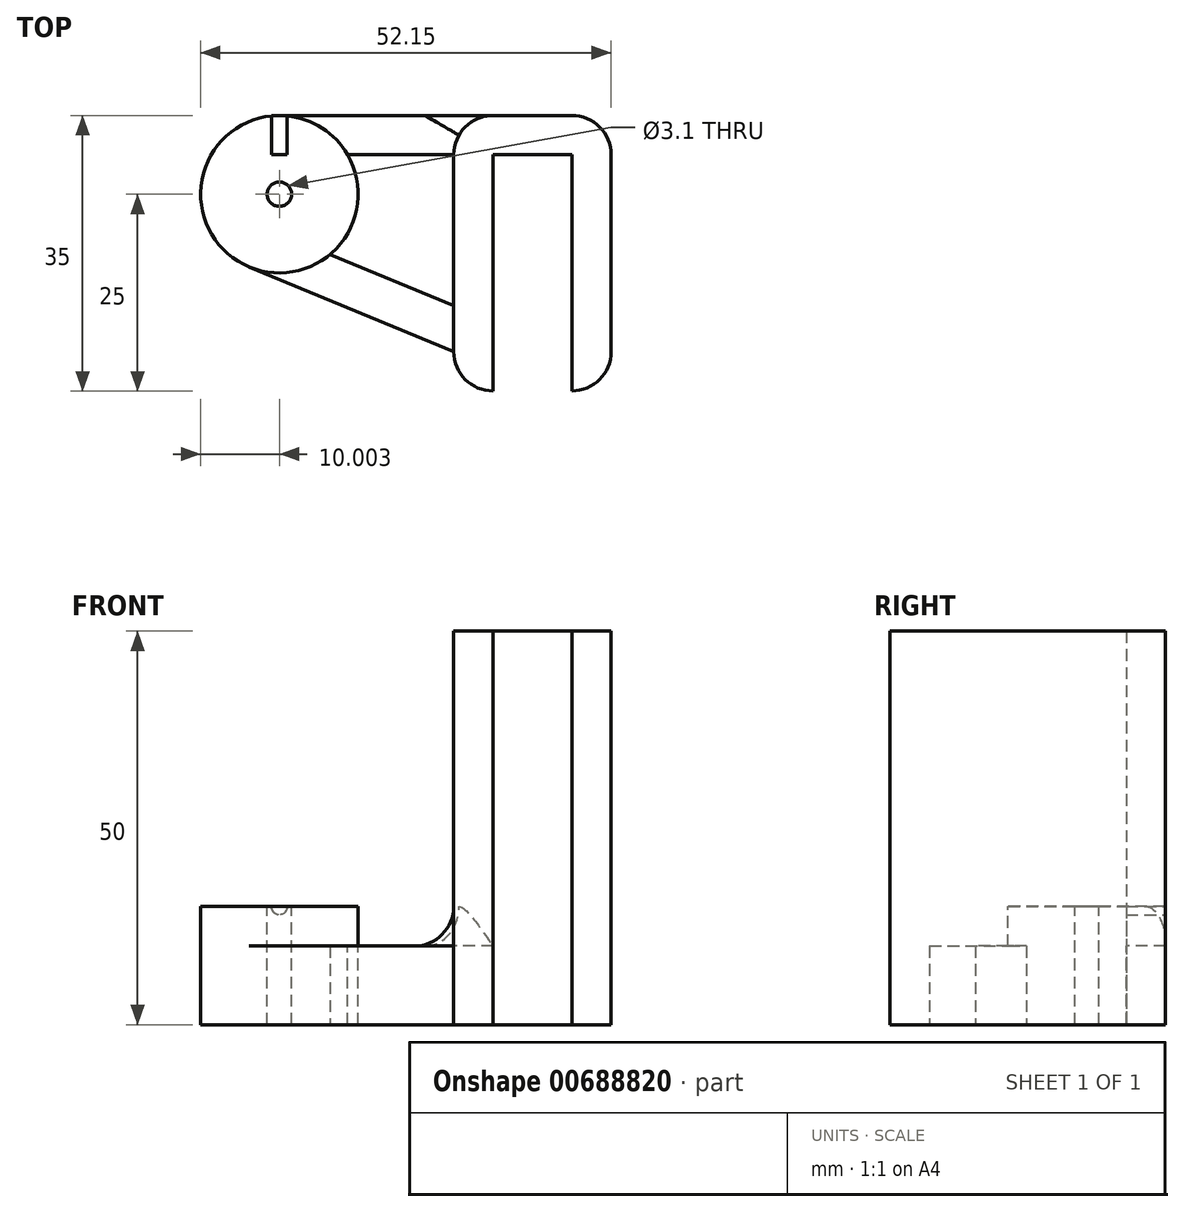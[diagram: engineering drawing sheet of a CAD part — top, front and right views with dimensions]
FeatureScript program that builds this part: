
annotation { "Feature Type Name" : "Feature", "Feature Type Description" : "" }
export const myFeature = defineFeature(function(context is Context, id is Id, definition is map)
    precondition{}
    {
        {
            var Q0;
            Q0=qCreatedBy(makeId("Top.planeOp"),FACE);
            var sketch = newSketch(context, id + "F0", { "sketchPlane" : qUnion([Q0])});
            skLineSegment(sketch, "E0.top", {"start": v(-72.5, 30) * mm, "end": v(-42.5, 30) * mm});
            skLineSegment(sketch, "E0.right", {"start": v(-22.5, 35) * mm, "end": v(-22.5, 30) * mm});
            skLineSegment(sketch, "E1.top", {"start": v(-27.5, 0) * mm, "end": v(-22.5, 0) * mm});
            skLineSegment(sketch, "E1.left", {"start": v(-27.5, 30) * mm, "end": v(-27.5, 0) * mm});
            skLineSegment(sketch, "E1.right", {"start": v(-22.5, 30) * mm, "end": v(-22.5, 0) * mm});
            skLineSegment(sketch, "E2.top", {"start": v(-42.5, 0) * mm, "end": v(-37.5, 0) * mm});
            skLineSegment(sketch, "E2.left", {"start": v(-42.5, 30) * mm, "end": v(-42.5, 0) * mm});
            skLineSegment(sketch, "E2.right", {"start": v(-37.5, 30) * mm, "end": v(-37.5, 0) * mm});
            skLineSegment(sketch, "E3.trimOffspring", {"start": v(-37.5, 30) * mm, "end": v(-27.5, 30) * mm});
            skLineSegment(sketch, "E4", {"start": v(-72.5, 35) * mm, "end": v(-72.5, 30) * mm});
            skLineSegment(sketch, "E5", {"start": v(-22.5, 35) * mm, "end": v(-72.5, 35) * mm});
            skLineSegment(sketch, "E6", {"start": v(-42.5, 30) * mm, "end": v(-42.5, 35) * mm});
            skSolve(sketch);
        }
        {
            var Q0;
            Q0=makeQuery(id+"F0.imprint","IMPRINT",FACE,{"disambiguationData":[TD([[makeQuery(id+"F0.imprint","IMPRINT",EDGE,{"derivedFrom":sQuery(id+"F0.wireOp",EDGE,"E0.top")}),1.0]])]});
            extrude(context, id + "F1", {"entities" : qUnion([Q0]), "depth" : 10 * mm, "offsetDistance" : 25 * mm});
        }
        {
            var Q0;
            Q0=makeQuery(id+"F1.opExtrude","CAP_FACE",FACE,{"disambiguationData":[OSD([sQuery(id+"F0.wireOp",EDGE,"E0.top"),sQuery(id+"F0.wireOp",EDGE,"E0.right"),sQuery(id+"F0.wireOp",EDGE,"E1.top"),sQuery(id+"F0.wireOp",EDGE,"E1.left"),sQuery(id+"F0.wireOp",EDGE,"E1.right"),sQuery(id+"F0.wireOp",EDGE,"E2.top"),sQuery(id+"F0.wireOp",EDGE,"E2.left"),sQuery(id+"F0.wireOp",EDGE,"E2.right"),sQuery(id+"F0.wireOp",EDGE,"E3.trimOffspring"),sQuery(id+"F0.wireOp",EDGE,"E4"),sQuery(id+"F0.wireOp",EDGE,"E5")])],"isStart":false});
            var sketch = newSketch(context, id + "F2", { "sketchPlane" : qUnion([Q0])});
            skCircle(sketch, "E7", {"center": v(-64.65, 25) * mm, "radius": 10 * mm});
            skCircle(sketch, "E8", {"center": v(-64.65, 25) * mm, "radius": 1.55 * mm});
            skSolve(sketch);
        }
        {
            var Q0;
            {var subQ0=sQuery(id+"F2.wireOp",EDGE,"E7");var subQ1=makeQuery(id+"F1.opExtrude","CAP_EDGE",EDGE,{"disambiguationData":[OSD([sQuery(id+"F0.wireOp",EDGE,"E0.top")])],"isStart":false});var subQ2=makeQuery(id+"F2.imprint","INTERSECT",VERTEX,{"disambiguationData":[OD(0.0)],"derivedFrom":[subQ1,subQ0]});Q0=makeQuery(id+"F2.imprint","IMPRINT",FACE,{"disambiguationData":[TD([[makeQuery(id+"F2.imprint","IMPRINT",EDGE,{"disambiguationData":[TD([[subQ2,1.0]])],"derivedFrom":subQ0}),1.0]])]});}
            var Q1;
            {var subQ0=sQuery(id+"F2.wireOp",EDGE,"E7");var subQ1=makeQuery(id+"F2.imprint","INTERSECT",VERTEX,{"derivedFrom":[makeQuery(id+"F1.opExtrude","CAP_EDGE",EDGE,{"disambiguationData":[OSD([sQuery(id+"F0.wireOp",EDGE,"E5")])],"isStart":false}),subQ0]});Q1=makeQuery(id+"F2.imprint","IMPRINT",FACE,{"disambiguationData":[TD([[makeQuery(id+"F2.imprint","IMPRINT",EDGE,{"disambiguationData":[TD([[subQ1,1.0]])],"derivedFrom":subQ0}),1.0]])]});}
            extrude(context, id + "F3", {"entities" : qUnion([Q0, Q1]), "operationType" : NewBodyOperationType.ADD, "oppositeDirection" : true, "depth" : 10 * mm, "offsetDistance" : 25 * mm, "hasSecondDirection" : true, "secondDirectionOppositeDirection" : false, "secondDirectionDepth" : 5 * mm});
        }
        {
            var Q0;
            {var subQ5=makeQuery(id+"F1.opExtrude","CAP_EDGE",EDGE,{"disambiguationData":[OSD([sQuery(id+"F0.wireOp",EDGE,"E4")])],"isStart":false});Q0=makeQuery(id+"F2.imprint","IMPRINT",FACE,{"disambiguationData":[TD([[makeQuery(id+"F2.imprint","IMPRINT",EDGE,{"derivedFrom":subQ5}),1.0]])]});}
            extrude(context, id + "F4", {"entities" : qUnion([Q0]), "operationType" : NewBodyOperationType.REMOVE, "oppositeDirection" : true, "depth" : 25 * mm, "offsetDistance" : 25 * mm});
        }
        {
            var Q0;
            {var subQ1=sQuery(id+"F0.wireOp",EDGE,"E0.right");Q0=makeQuery(id+"F0.imprint","IMPRINT",FACE,{"disambiguationData":[TD([[makeQuery(id+"F0.imprint","IMPRINT",EDGE,{"derivedFrom":subQ1}),-1.0]])]});}
            extrude(context, id + "F5", {"entities" : qUnion([Q0]), "operationType" : NewBodyOperationType.ADD, "depth" : 50 * mm, "offsetDistance" : 25 * mm});
        }
        {
            var Q0;
            Q0=makeQuery(id+"F5.opExtrude","SWEPT_EDGE",EDGE,{"disambiguationData":[OSD([sQuery(id+"F0.wireOp",EDGE,"E0.top"),sQuery(id+"F0.wireOp",EDGE,"E2.left")])]});
            var Q1;
            Q1=makeQuery(id+"F5.opExtrude","SWEPT_EDGE",EDGE,{"disambiguationData":[OSD([sQuery(id+"F0.wireOp",EDGE,"E0.right"),sQuery(id+"F0.wireOp",EDGE,"E5")])]});
            var Q2;
            Q2=makeQuery(id+"F5.opExtrude","SWEPT_EDGE",EDGE,{"disambiguationData":[OSD([sQuery(id+"F0.wireOp",EDGE,"E5"),sQuery(id+"F0.wireOp",EDGE,"CNXITYnM-IfMt-CwRq-EaPs-oMCtDQrPVvlV")])]});
            var Q3;
            Q3=makeQuery(id+"F5.opExtrude","SWEPT_EDGE",EDGE,{"disambiguationData":[OSD([sQuery(id+"F0.wireOp",EDGE,"E1.top"),sQuery(id+"F0.wireOp",EDGE,"E1.right")])]});
            fillet(context, id + "F6", {"entities" : qUnion([Q0, Q1, Q2, Q3]), "radius" : 5 * mm, "tangentPropagation" : true, "allowEdgeOverflow" : false});
        }
        {
            var Q0;
            {var subQ0=sQuery(id+"F0.wireOp",EDGE,"E6");var subQ1=sQuery(id+"F0.wireOp",EDGE,"E5");Q0=makeQuery(id+"F5.boolean.opBoolean","MERGE",FACE,{"derivedFrom":[makeQuery(id+"F3.boolean.opBoolean","MERGE",FACE,{"derivedFrom":[makeQuery(id+"F1.opExtrude","CAP_FACE",FACE,{"disambiguationData":[OSD([sQuery(id+"F0.wireOp",EDGE,"E0.top"),sQuery(id+"F0.wireOp",EDGE,"E4"),subQ1,subQ0])],"isStart":true}),makeQuery(id+"F3.opExtrude","CAP_FACE",FACE,{"disambiguationData":[OSD([sQuery(id+"F2.wireOp",EDGE,"E7")])],"isStart":false})]}),makeQuery(id+"F5.opExtrude","CAP_FACE",FACE,{"disambiguationData":[OSD([sQuery(id+"F0.wireOp",EDGE,"E0.right"),sQuery(id+"F0.wireOp",EDGE,"E1.top"),sQuery(id+"F0.wireOp",EDGE,"E1.left"),sQuery(id+"F0.wireOp",EDGE,"E1.right"),sQuery(id+"F0.wireOp",EDGE,"E2.top"),sQuery(id+"F0.wireOp",EDGE,"E2.left"),sQuery(id+"F0.wireOp",EDGE,"E2.right"),sQuery(id+"F0.wireOp",EDGE,"E3.trimOffspring"),subQ1,subQ0])],"isStart":true})]});}
            var sketch = newSketch(context, id + "F7", { "sketchPlane" : qUnion([Q0])});
            skLineSegment(sketch, "E9", {"start": v(-42.5, -5) * mm, "end": v(-68.47, -15.76) * mm});
            skLineSegment(sketch, "E10", {"start": v(-58.22, -17.34) * mm, "end": v(-42.5, -10.83) * mm});
            skSolve(sketch);
        }
        {
            var Q0;
            {var subQ0=sQuery(id+"F7.wireOp",EDGE,"E9");Q0=makeQuery(id+"F7.imprint","IMPRINT",FACE,{"disambiguationData":[TD([[makeQuery(id+"F7.imprint","IMPRINT",EDGE,{"derivedFrom":subQ0}),1.0]])]});}
            extrude(context, id + "F8", {"entities" : qUnion([Q0]), "operationType" : NewBodyOperationType.ADD, "oppositeDirection" : true, "depth" : 10 * mm, "offsetDistance" : 25 * mm});
        }
        {
            var Q0;
            {var subQ0=sQuery(id+"F0.wireOp",EDGE,"E5");Q0=makeQuery(id+"F5.boolean.opBoolean","MERGE",FACE,{"derivedFrom":[makeQuery(id+"F1.opExtrude","SWEPT_FACE",FACE,{"disambiguationData":[OSD([subQ0])]}),makeQuery(id+"F5.opExtrude","SWEPT_FACE",FACE,{"disambiguationData":[OSD([subQ0])]})]});}
            var sketch = newSketch(context, id + "F9", { "sketchPlane" : qUnion([Q0])});
            skCircle(sketch, "E11", {"center": v(64.65, 14.97) * mm, "radius": 1 * mm});
            skSolve(sketch);
        }
        {
            var Q0;
            Q0=makeQuery(id+"F9.imprint","IMPRINT",FACE,{"disambiguationData":[TD([[makeQuery(id+"F9.imprint","IMPRINT",EDGE,{"derivedFrom":sQuery(id+"F9.wireOp",EDGE,"E11")}),1.0]])]});
            extrude(context, id + "F10", {"entities" : qUnion([Q0]), "operationType" : NewBodyOperationType.REMOVE, "oppositeDirection" : true, "depth" : 5 * mm, "offsetDistance" : 25 * mm});
        }
        {
            var Q0;
            Q0=makeQuery(id+"F5.opExtrude","SWEPT_FACE",FACE,{"disambiguationData":[OSD([sQuery(id+"F0.wireOp",EDGE,"E2.left"),sQuery(id+"F0.wireOp",EDGE,"E6")])]});
            var Q1;
            Q1=sQuery(id+"F2.wireOp",VERTEX,"E7.center");
            cPlane(context, id + "F11", {"entities" : qUnion([Q0, Q1]), "cplaneType" : CPlaneType.PLANE_POINT, "offset" : 25 * mm, "width" : 150 * mm, "height" : 150 * mm});
        }
        {
            var Q0;
            Q0=qCreatedBy(id+"F11.planeOp",FACE);
            var sketch = newSketch(context, id + "F12", { "sketchPlane" : qUnion([Q0])});
            skLineSegment(sketch, "E12", {"start": v(-25, 10) * mm, "end": v(-25, -18.65) * mm});
            skSolve(sketch);
        }
        {
            var Q0;
            {var subQ0=sQuery(id+"F0.wireOp",EDGE,"E5");var subQ1=sQuery(id+"F0.wireOp",EDGE,"E6");var subQ2=sQuery(id+"F0.wireOp",EDGE,"E0.top");var subQ3=makeQuery(id+"F1.opExtrude","CAP_FACE",FACE,{"disambiguationData":[OSD([subQ2,sQuery(id+"F0.wireOp",EDGE,"E4"),subQ0,subQ1])],"isStart":false});Q0=makeQuery(id+"F6.opFillet","BLEND_EDGE",EDGE,{"blendedFrom":[makeQuery(id+"F5.opExtrude","SWEPT_EDGE",EDGE,{"disambiguationData":[OSD([subQ0,subQ1])]}),makeQuery(id+"F3.boolean.opBoolean","SPLIT",FACE,{"disambiguationData":[TD([makeQuery(id+"F1.opExtrude","SWEPT_FACE",FACE,{"disambiguationData":[OSD([subQ2])]})])],"derivedFrom":subQ3})],"blendedInto":[makeQuery(id+"F3.boolean.opBoolean","SPLIT",FACE,{"disambiguationData":[TD([makeQuery(id+"F1.opExtrude","SWEPT_FACE",FACE,{"disambiguationData":[OSD([subQ2])]})])],"derivedFrom":subQ3})]});}
            var Q1;
            Q1=makeQuery(id+"F8.opExtrude","CAP_EDGE",EDGE,{"disambiguationData":[OSD([sQuery(id+"F0.wireOp",EDGE,"E2.left"),sQuery(id+"F0.wireOp",EDGE,"E6")])],"isStart":false});
            fillet(context, id + "F13", {"entities" : qUnion([Q0, Q1]), "radius" : 5 * mm, "tangentPropagation" : true, "allowEdgeOverflow" : false});
        }
    });
